# Revit family: Furniture_Office-Desks&Tables_Dandent_DTV1003_Computer-Cart
name_source: partatom
category: Furniture
revit_build: Autodesk Revit 2017 (Build: 20190508_0315(x64)
units: mm (PartAtom-declared; Revit-internal decimal feet)

## family parameters
Always vertical = Yes
Cut with Voids When Loaded = No
OmniClass Number = 23.40.70.11.14.21
OmniClass Title = Health Care Furniture
Room Calculation Point = No
Shared = No
Work Plane-Based = No

## types (1)
- Computer cart - DTV1003
    AssetType = Movable
    BIMObjectName = Furniture_Office-Desks&Tables_Dandent_DTV1003_Computer-Cart
    Brand = Dandent
    Category = Computer furniture
    Color = Grey
    ConvergoRefNr = 0151-1909-0013-SE
    Cost = 0 $
    Description = Computer trolley for flexible placement of computer workspace, for one or two screens.
Easy to move, raise and lower.
    DurationUnit = Year
    Features = Electrical raising and lowering, lockable wheels
    Finish = Table available in white, birch or beech laminate
    IfcExportAs = IfcFurnishingElementType
    IfcExportType = TABLE
    MainColor = Grey
    Manufacturer = Dandent
    ManufacturerName = Dandent
    ManufacturerURL = https://www.dandent.se
    Material = Wood, metal, plastic
    Model = Computer cart - DTV1003
    NBSDescription = Medical desks, tables and worktops
    NBSReference = 45-35-20/340
    Name = Dandent_DTV1003_Computer-Cart
    NominalDepth = 610 mm
    NominalHeight = 1000 mm  [stored 3.28084 ft]
    NominalLength = 700 mm  [stored 2.29659 ft]
    Product data url = https://www.bimobject.com
    ProductDatasheet = https://www.dandent.se
    ProductInformation = Computer trolley for flexible placement of computer workspace, for one or two screens.
Easy to move, raise and lower.
    Shape = Sculptured
    Size = 700x610x1000 mm
    TableMainMaterial = Grey steel
    URL = https://www.dandent.se
    Uniclass2 = Pr_40_50
    Uniclass2015Description = Medical desks, tables and worktops
    Uniclass2015Reference = Pr_40_50_52
    Version = 1
    VersionDate = 12/09/2019
    WarrantyDurationUnit = Year

note: [stored X ft] marks values corroborated as IEEE doubles in the binary element streams (Revit-internal decimal feet)

## geometry (parser evidence)
native form markers: Sweep x7
no freeform markers — native parametric forms only
